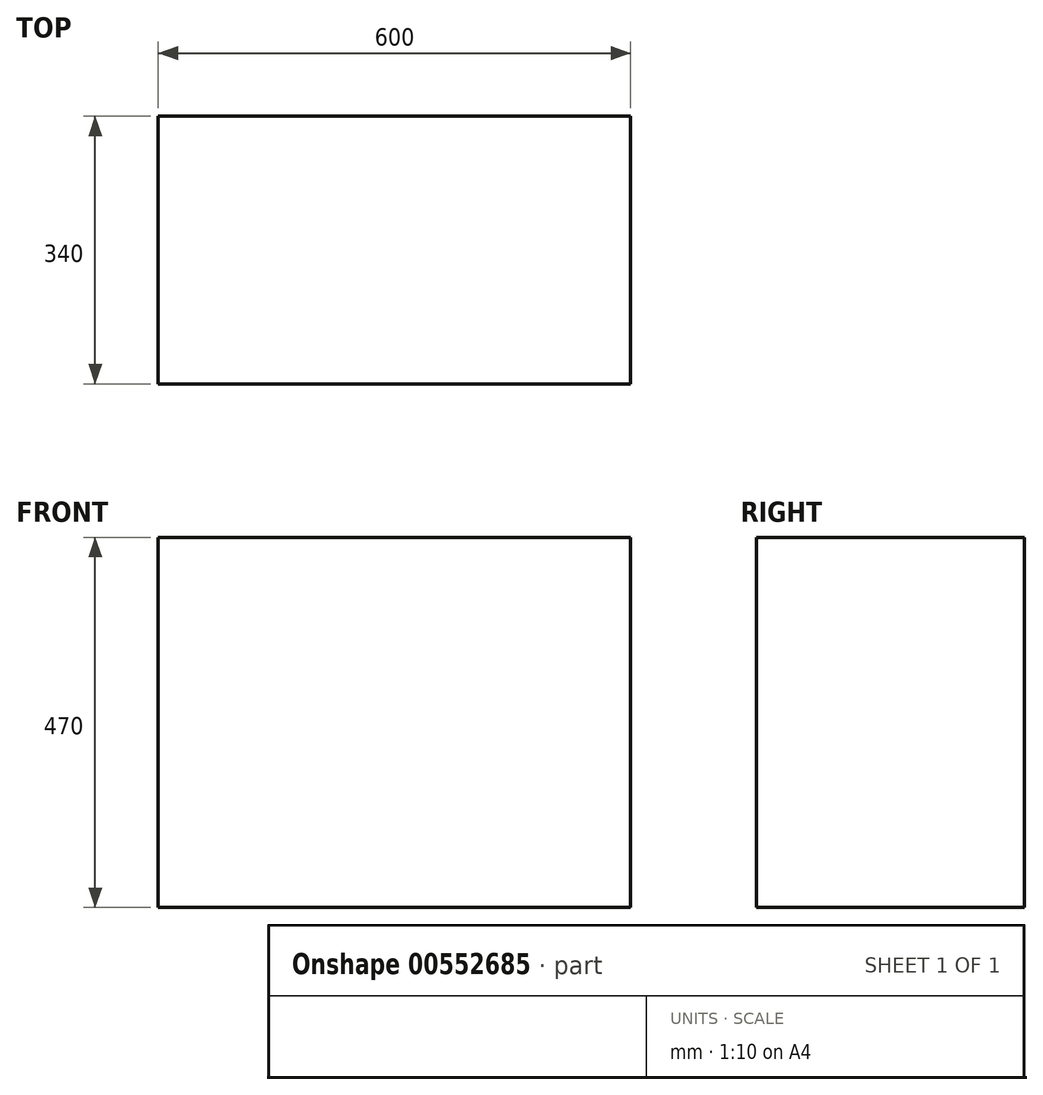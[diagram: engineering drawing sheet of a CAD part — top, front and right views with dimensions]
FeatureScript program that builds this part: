
annotation { "Feature Type Name" : "Feature", "Feature Type Description" : "" }
export const myFeature = defineFeature(function(context is Context, id is Id, definition is map)
    precondition{}
    {
        {
            var Q0;
            Q0=qCreatedBy(makeId("Front.planeOp"),FACE);
            var sketch = newSketch(context, id + "F0", { "sketchPlane" : qUnion([Q0])});
            skLineSegment(sketch, "E0.bottom", {"start": v(300, 235) * mm, "end": v(-300, 235) * mm});
            skLineSegment(sketch, "E0.top", {"start": v(300, -235) * mm, "end": v(-300, -235) * mm});
            skLineSegment(sketch, "E0.left", {"start": v(300, 235) * mm, "end": v(300, -235) * mm});
            skLineSegment(sketch, "E0.right", {"start": v(-300, 235) * mm, "end": v(-300, -235) * mm});
            skPoint(sketch, "E0.middle", {"position": v(0, 0) * mm});
            skSolve(sketch);
        }
        {
            var Q0;
            Q0 = qSketchRegion(id + "F0", true);
            extrude(context, id + "F1", {"entities" : qUnion([Q0]), "oppositeDirection" : true, "depth" : 340 * mm, "offsetDistance" : 25 * mm});
        }
    });
